# Revit family: EVE4X
name_source: partatom
category: Lighting Fixtures
units: mm (PartAtom-declared; Revit-internal decimal feet)

## family parameters
Cut with Voids When Loaded = No
Host = Face
Light Source = No
OmniClass Number = 23.80.70.11.21
OmniClass Title = Emergency Lighting
Part Type = Normal
Room Calculation Point = No
Round Connector Dimension = Use Diameter
Shared = No

## types (1)
- EVE4X
    Apparent Load = 2 VA
    Application = The EVE4X is designed for indoor or outdoor wet or dusty
environments requiring corrosion resistant, UL50 type 4X exit signs
with energy-saving, long-life LEDs. Available in AC only or emergency
operation which includes a nickel metal hydride(NiMH) battery and
provides a full 90 minutes of emergency exit illumination in the event
of power failure. Includes a constant current charger. The EVE accepts
120/277VAC input at 60Hz with a self-diagnostic option.
    Certification = Certified to UL924 Wet Location Standards
NFPA 101 (Life Safety Code)
NFPA 70 (National Electrical Code)
    Default Elevation = 48.000"
    Description = EVE4X Series LED exit signs meet NEMA 4X IP66 standards, the housing is watertight and corrosion resistant, and is designed for Indoor or Outdoor application.
    End = C : C1
    Features = External push-to-test switch and AC-on indicator
• Battery re-charge within 24 hours
• AC Lock-out battery circuit
• Low voltage battery disconnect
• UL 50 type 4X units for indoor/outdoor use
• Suitable for use in wet locations
• Oil-resistant gasket for watertight/dust-tight seal
• High-impact, corrosion-resistant polycarbonate housing
• Easy installation
• Bright, even illumination
• Exceeds NFPA 101 illumination requirements
• Red and green letters
• Snap-in chevron type directional arrows
    Finish = White
    Glass = light Glass
    Holder Material = Steel
    Lamp = LED Lamp
    Lens = Paint - Gray Smooth
    Load Classification = Lighting
    Manufacturer = DUAL-LITE
    Model = CLS
    Type Comments = Exit Light
    URL = https://www.currentlighting.com
    Wall Plate Material = Black
    Warranty = EVE4X Full 5 year warranty
Battery, 3 years full, 7 years pro-rata
    Wattage Comments = 2.00 W
    Watts = 2 W
    Ïnstallation = EVE4X Series exit signs are designed to mount to the wall through four
1/4” integral mounting holes in the unit housing. Mounting hardware is
supplied by others. Units must be surface wired for utility power input.
Housings are easily drilled or punched to accept sealed conduit hubs
(supplied by others).

## geometry (parser evidence)
native form markers: Blend x8, Sweep x4
no freeform markers — native parametric forms only
